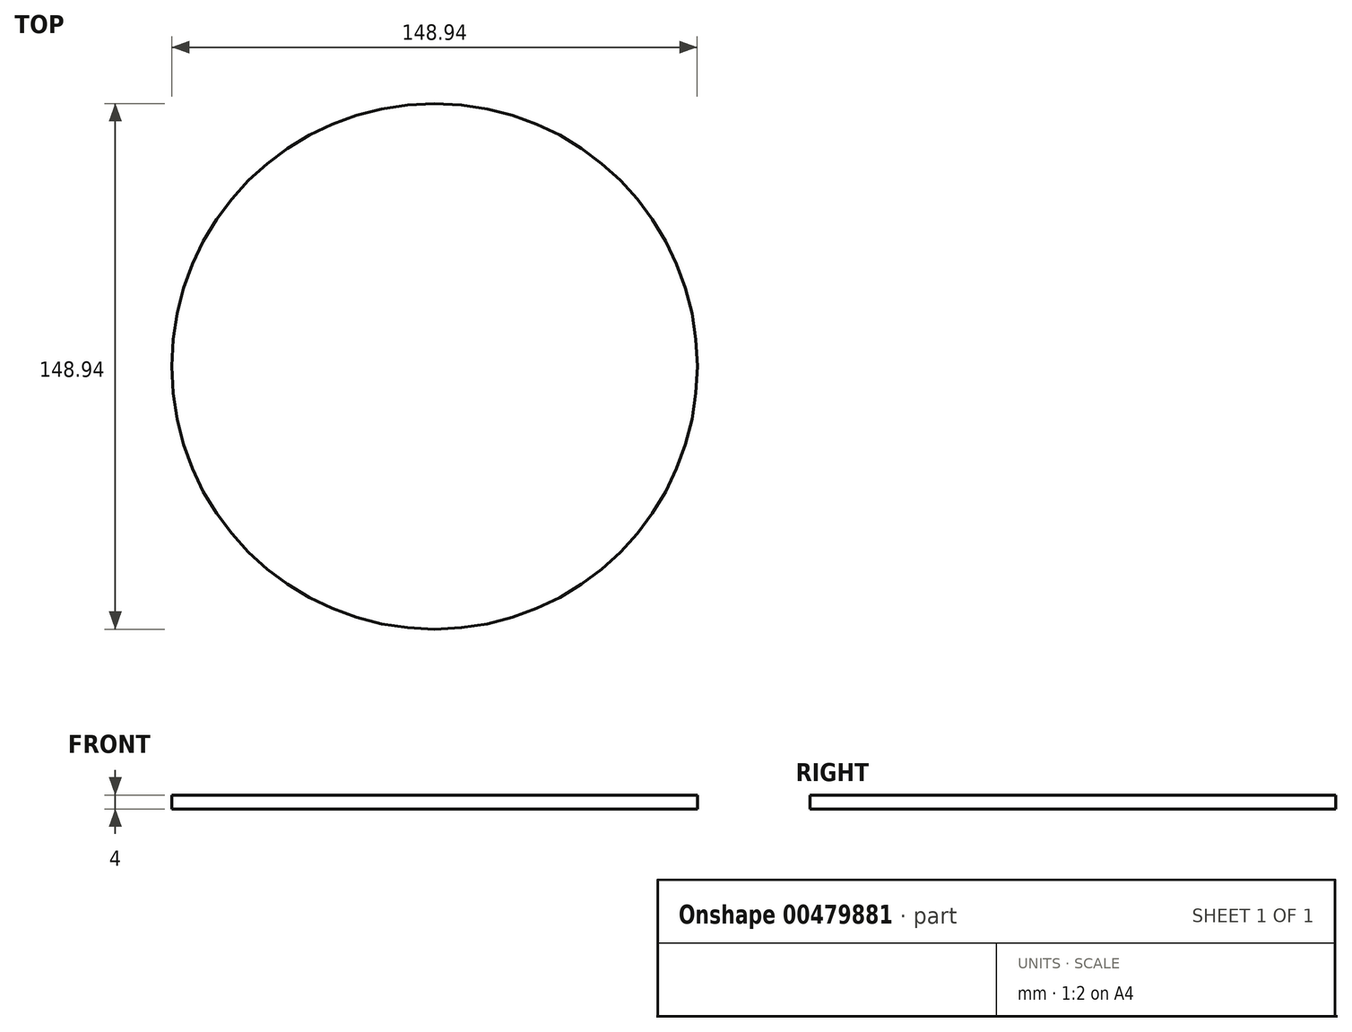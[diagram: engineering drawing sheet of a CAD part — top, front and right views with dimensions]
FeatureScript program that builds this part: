
annotation { "Feature Type Name" : "Feature", "Feature Type Description" : "" }
export const myFeature = defineFeature(function(context is Context, id is Id, definition is map)
    precondition{}
    {
        {
            var Q0;
            Q0=qCreatedBy(makeId("Top.planeOp"),FACE);
            var sketch = newSketch(context, id + "F0", { "sketchPlane" : qUnion([Q0])});
            skCircle(sketch, "E0", {"center": v(0, 0) * mm, "radius": 74.47 * mm});
            skSolve(sketch);
        }
        {
            var Q0;
            Q0 = qSketchRegion(id + "F0", true);
            extrude(context, id + "F1", {"entities" : qUnion([Q0]), "depth" : 4 * mm});
        }
    });
